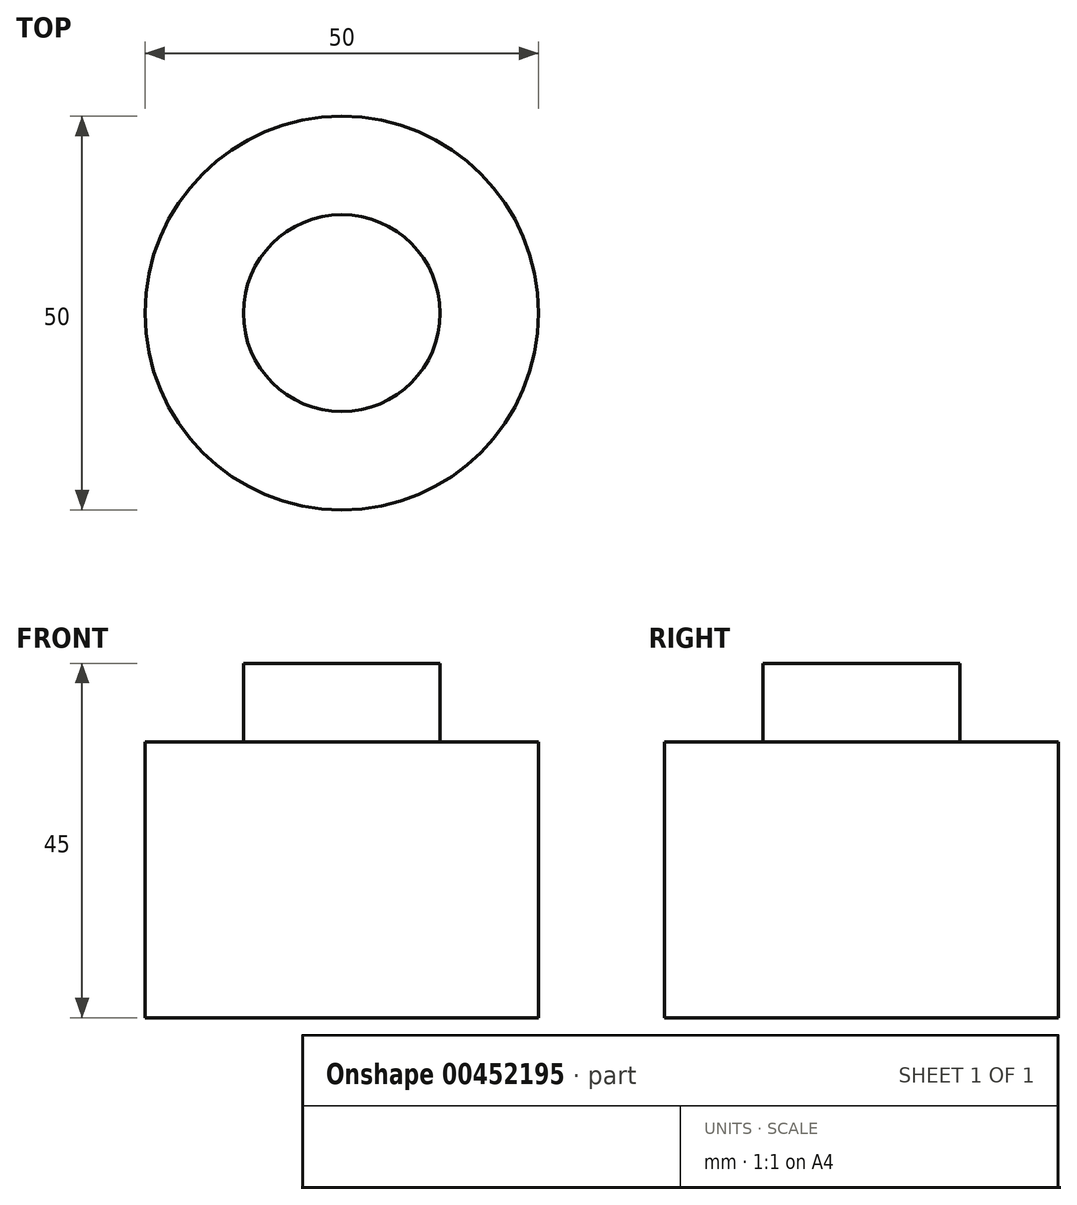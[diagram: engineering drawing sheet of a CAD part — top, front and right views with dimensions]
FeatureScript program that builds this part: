
annotation { "Feature Type Name" : "Feature", "Feature Type Description" : "" }
export const myFeature = defineFeature(function(context is Context, id is Id, definition is map)
    precondition{}
    {
        {
            var Q0;
            Q0=qCreatedBy(makeId("Top.planeOp"),FACE);
            cPlane(context, id + "F0", {"entities" : qUnion([Q0]), "cplaneType" : CPlaneType.OFFSET, "offset" : 35 * mm, "width" : 150 * mm, "height" : 150 * mm});
        }
        {
            var Q0;
            Q0=qCreatedBy(makeId("Top.planeOp"),FACE);
            var sketch = newSketch(context, id + "F1", { "sketchPlane" : qUnion([Q0])});
            skCircle(sketch, "E0", {"center": v(0, 0) * mm, "radius": 25 * mm});
            skSolve(sketch);
        }
        {
            var Q0;
            Q0=makeQuery(id+"F1.imprint","IMPRINT",FACE,{"disambiguationData":[TD([[makeQuery(id+"F1.imprint","IMPRINT",EDGE,{"derivedFrom":sQuery(id+"F1.wireOp",EDGE,"E0")}),1.0]])]});
            extrude(context, id + "F2", {"entities" : qUnion([Q0]), "depth" : 25 * mm});
        }
        {
            var Q0;
            Q0=makeQuery(id+"F2.opExtrude","CAP_FACE",FACE,{"disambiguationData":[OSD([sQuery(id+"F1.wireOp",EDGE,"E0")])],"isStart":false});
            extrude(context, id + "F3", {"entities" : qUnion([Q0]), "operationType" : NewBodyOperationType.ADD, "depth" : 10 * mm});
        }
        {
            var Q0;
            Q0=qCreatedBy(id+"F0.planeOp",FACE);
            var sketch = newSketch(context, id + "F4", { "sketchPlane" : qUnion([Q0])});
            skCircle(sketch, "E1", {"center": v(0, 0) * mm, "radius": 12.5 * mm});
            skSolve(sketch);
        }
        {
            var Q0;
            Q0=makeQuery(id+"F4.imprint","IMPRINT",FACE,{"disambiguationData":[TD([[makeQuery(id+"F4.imprint","IMPRINT",EDGE,{"derivedFrom":sQuery(id+"F4.wireOp",EDGE,"E1")}),1.0]])]});
            extrude(context, id + "F5", {"entities" : qUnion([Q0]), "operationType" : NewBodyOperationType.ADD, "depth" : 10 * mm});
        }
        {
            var Q0;
            Q0=qCreatedBy(id+"F0.planeOp",FACE);
            cPlane(context, id + "F6", {"entities" : qUnion([Q0]), "cplaneType" : CPlaneType.OFFSET, "offset" : 10 * mm, "width" : 150 * mm, "height" : 150 * mm});
        }
    });
